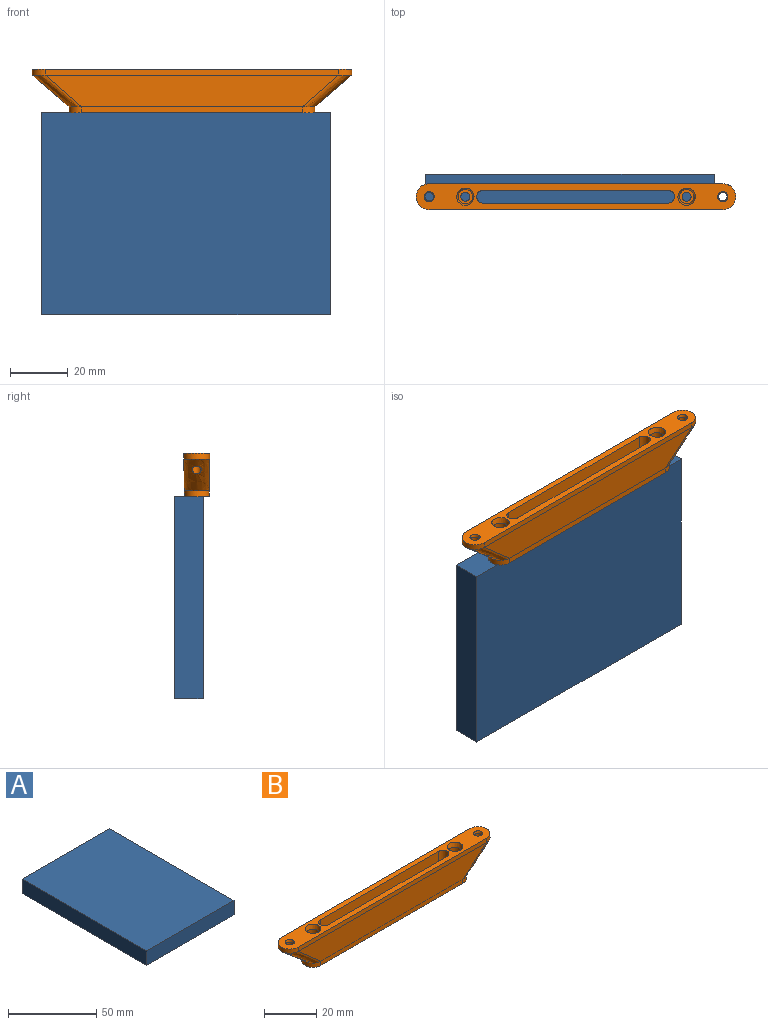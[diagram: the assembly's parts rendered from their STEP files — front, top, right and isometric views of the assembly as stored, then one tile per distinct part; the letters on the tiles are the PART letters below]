
ASSEMBLY  parts=2 mates=1
PART A: 6 faces, bbox 70x100x10 mm
  f0: plane 70x10mm, normal (0,1,0), area 700mm2, adj f1,f3,f4,f5
  f1: plane 100x10mm, normal (-1,0,0), area 1000mm2, adj f0,f2,f4,f5
  f2: plane 70x10mm, normal (0,-1,0), area 700mm2, adj f1,f3,f4,f5
  f3: plane 100x10mm, normal (1,0,0), area 1000mm2, adj f0,f2,f4,f5
  f4: plane 100x70mm, normal (0,0,1), area 7000mm2, adj f0,f1,f2,f3
  f5: plane 100x70mm, normal (0,0,-1), area 7000mm2, adj f0,f1,f2,f3
PART B: 30 faces, bbox 110.6x9x15 mm
  f0: plane 85.1x8.5mm, normal (0,0,-1), area 389.2mm2, adj f4,f5,f6,f7,f14,f17,f22,f23
  f1: plane 110.6x9mm, normal (0,0,1), area 598.6mm2, adj f8,f9,f10,f11,f22,f23,f24,f25
  f2: bspline ~106.72x11mm, area 184.5mm2, adj f7,f10,f12,f13,f21
  f3: bspline ~106.72x11mm, area 184.5mm2, adj f5,f8,f12,f13,f20
  f4: plane 76.6x2mm, normal (0,1,0), area 153.2mm2, adj f0,f5,f7,f13
  f5: cylinder r=4.25mm len=8.5mm, axis (0,0,-1), area 26.7mm2, adj f0,f3,f4,f6
  f6: plane 76.6x2mm, normal (0,-1,0), area 153.2mm2, adj f0,f5,f7,f12
  f7: cylinder r=4.25mm len=8.5mm, axis (0,0,-1), area 26.7mm2, adj f0,f2,f4,f6
  f8: cylinder r=4.5mm len=9mm, axis (0,0,1), area 28.3mm2, adj f1,f3,f9,f11
  f9: plane 101.6x2mm, normal (0,-1,0), area 203.2mm2, adj f1,f8,f10,f12
  f10: cylinder r=4.5mm len=9mm, axis (0,0,1), area 28.3mm2, adj f1,f2,f9,f11
  f11: plane 101.6x2mm, normal (0,1,0), area 203.2mm2, adj f1,f8,f10,f13
  f12: plane 101.6x11mm, normal (0,-1,-0.02), area 980.4mm2, adj f2,f3,f6,f9
  f13: plane 101.6x11mm, normal (0,1,-0.02), area 980.4mm2, adj f2,f3,f4,f11
  f14: cylinder r=1.55mm len=3.1mm, axis (0,0,1), area 9.7mm2, adj f0,f15
  f15: plane 5x5mm, normal (0,0,1), area 12.1mm2, adj f14,f16
  f16: cylinder r=2.5mm len=12mm, axis (0,0,1), area 188.5mm2, adj f15,f28
  f17: cylinder r=1.55mm len=3.1mm, axis (0,0,1), area 9.7mm2, adj f0,f18
  f18: plane 5x5mm, normal (0,0,1), area 12.1mm2, adj f17,f19
  f19: cylinder r=2.5mm len=12mm, axis (0,0,1), area 188.5mm2, adj f18,f29
  f20: cylinder r=1.5mm len=6.18mm, axis (0,0,1), area 45mm2, adj f3,f26
  f21: cylinder r=1.5mm len=6.18mm, axis (0,0,1), area 44.9mm2, adj f2,f27
  f22: cylinder r=2.25mm len=15mm, axis (0,0,-1), area 106mm2, adj f0,f1,f23,f25
  f23: plane 63.93x15mm, normal (0,1,0), area 958.9mm2, adj f0,f1,f22,f24
  f24: cylinder r=2.25mm len=15mm, axis (0,0,-1), area 106mm2, adj f0,f1,f23,f25
  f25: plane 63.93x15mm, normal (0,-1,0), area 958.9mm2, adj f0,f1,f22,f24
  f26: cone r=1.5mm half-angle=14deg, axis (0,0,1), area 10.5mm2, adj f1,f20
  f27: cone r=1.5mm half-angle=14deg, axis (0,0,1), area 10.5mm2, adj f1,f21
  f28: cone r=2.5mm half-angle=14deg, axis (0,0,1), area 35.6mm2, adj f1,f16
  f29: cone r=2.5mm half-angle=14deg, axis (0,0,1), area 35.6mm2, adj f1,f19
PLACE A rot(axis=(0.58,-0.58,0.58),120deg) t=(-75.54,9.04,54.33)mm
PLACE B t=(-76.61,1.27,93.77)mm
MATE planar B.f0 <-> A.f3  axis (0,0,-1) through (-76.51,1.27,93.77)mm
